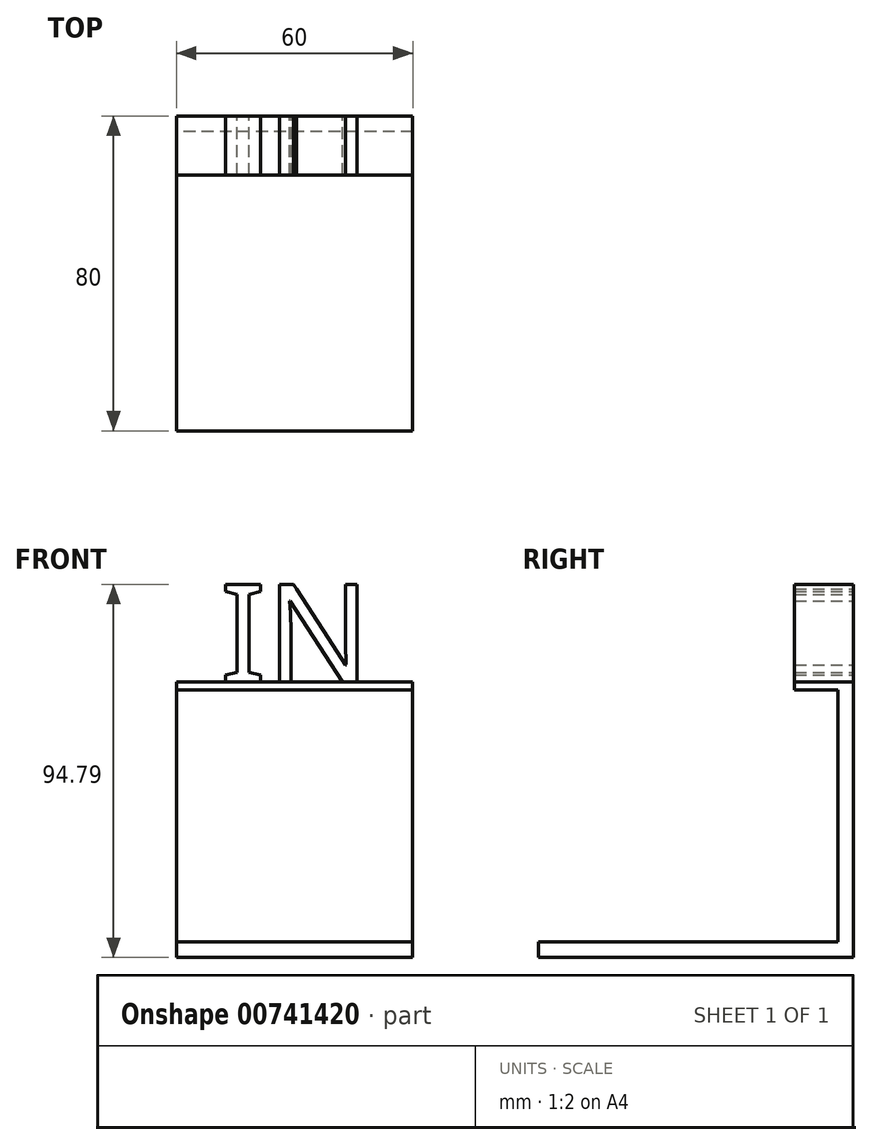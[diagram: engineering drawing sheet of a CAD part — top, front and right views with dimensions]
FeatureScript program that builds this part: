
annotation { "Feature Type Name" : "Feature", "Feature Type Description" : "" }
export const myFeature = defineFeature(function(context is Context, id is Id, definition is map)
    precondition{}
    {
        {
            var Q0;
            Q0=qCreatedBy(makeId("Front.planeOp"),FACE);
            var sketch = newSketch(context, id + "F0", { "sketchPlane" : qUnion([Q0])});
            skLineSegment(sketch, "E0.bottom", {"start": v(-28.33, 24.57) * mm, "end": v(31.67, 24.57) * mm});
            skLineSegment(sketch, "E0.top", {"start": v(-28.33, -45.43) * mm, "end": v(31.67, -45.43) * mm});
            skLineSegment(sketch, "E0.left", {"start": v(-28.33, 24.57) * mm, "end": v(-28.33, -45.43) * mm});
            skLineSegment(sketch, "E0.right", {"start": v(31.67, 24.57) * mm, "end": v(31.67, -45.43) * mm});
            skSolve(sketch);
        }
        {
            var Q0;
            Q0=makeQuery(id+"F0.imprint","IMPRINT",FACE,{"disambiguationData":[TD([[makeQuery(id+"F0.imprint","IMPRINT",EDGE,{"derivedFrom":sQuery(id+"F0.wireOp",EDGE,"E0.bottom")}),-1.0]])]});
            extrude(context, id + "F1", {"entities" : qUnion([Q0]), "depth" : 4 * mm, "offsetDistance" : 25 * mm});
        }
        {
            var Q0;
            Q0=qCreatedBy(makeId("Front.planeOp"),FACE);
            var sketch = newSketch(context, id + "F2", { "sketchPlane" : qUnion([Q0])});
            skLineSegment(sketch, "E1.bottom", {"start": v(-28.33, 24.57) * mm, "end": v(31.67, 24.57) * mm});
            skLineSegment(sketch, "E1.top", {"start": v(-28.33, 22.57) * mm, "end": v(31.67, 22.57) * mm});
            skLineSegment(sketch, "E1.left", {"start": v(-28.33, 24.57) * mm, "end": v(-28.33, 22.57) * mm});
            skLineSegment(sketch, "E1.right", {"start": v(31.67, 24.57) * mm, "end": v(31.67, 22.57) * mm});
            skSolve(sketch);
        }
        {
            var Q0;
            Q0 = qSketchRegion(id + "F2", true);
            extrude(context, id + "F3", {"entities" : qUnion([Q0]), "operationType" : NewBodyOperationType.ADD, "depth" : 15 * mm, "offsetDistance" : 25 * mm});
        }
        {
            var Q0;
            Q0=qCreatedBy(makeId("Front.planeOp"),FACE);
            var sketch = newSketch(context, id + "F4", { "sketchPlane" : qUnion([Q0])});
            skLineSegment(sketch, "E2.bottom", {"start": v(-28.33, -41.43) * mm, "end": v(31.67, -41.43) * mm});
            skLineSegment(sketch, "E2.top", {"start": v(-28.33, -45.43) * mm, "end": v(31.67, -45.43) * mm});
            skLineSegment(sketch, "E2.left", {"start": v(-28.33, -41.43) * mm, "end": v(-28.33, -45.43) * mm});
            skLineSegment(sketch, "E2.right", {"start": v(31.67, -41.43) * mm, "end": v(31.67, -45.43) * mm});
            skSolve(sketch);
        }
        {
            var Q0;
            Q0 = qSketchRegion(id + "F4", true);
            extrude(context, id + "F5", {"entities" : qUnion([Q0]), "operationType" : NewBodyOperationType.ADD, "depth" : 80 * mm, "offsetDistance" : 25 * mm});
        }
        {
            var Q0;
            Q0=qCreatedBy(makeId("Front.planeOp"),FACE);
            var sketch = newSketch(context, id + "F6", { "sketchPlane" : qUnion([Q0])});
            skText(sketch, "E3", { "text": "IN", "fontName": "NotoSans-Regular.ttf"});
            const initialGuessF6  = {"E3": [-0.01733, 0.02457, 1, 0, 0.025]};
            skSetInitialGuess(sketch, initialGuessF6);
            skSolve(sketch);
        }
        {
            var Q0;
            Q0 = qSketchRegion(id + "F6", true);
            extrude(context, id + "F7", {"entities" : qUnion([Q0]), "operationType" : NewBodyOperationType.ADD, "depth" : 15 * mm, "offsetDistance" : 25 * mm});
        }
    });
